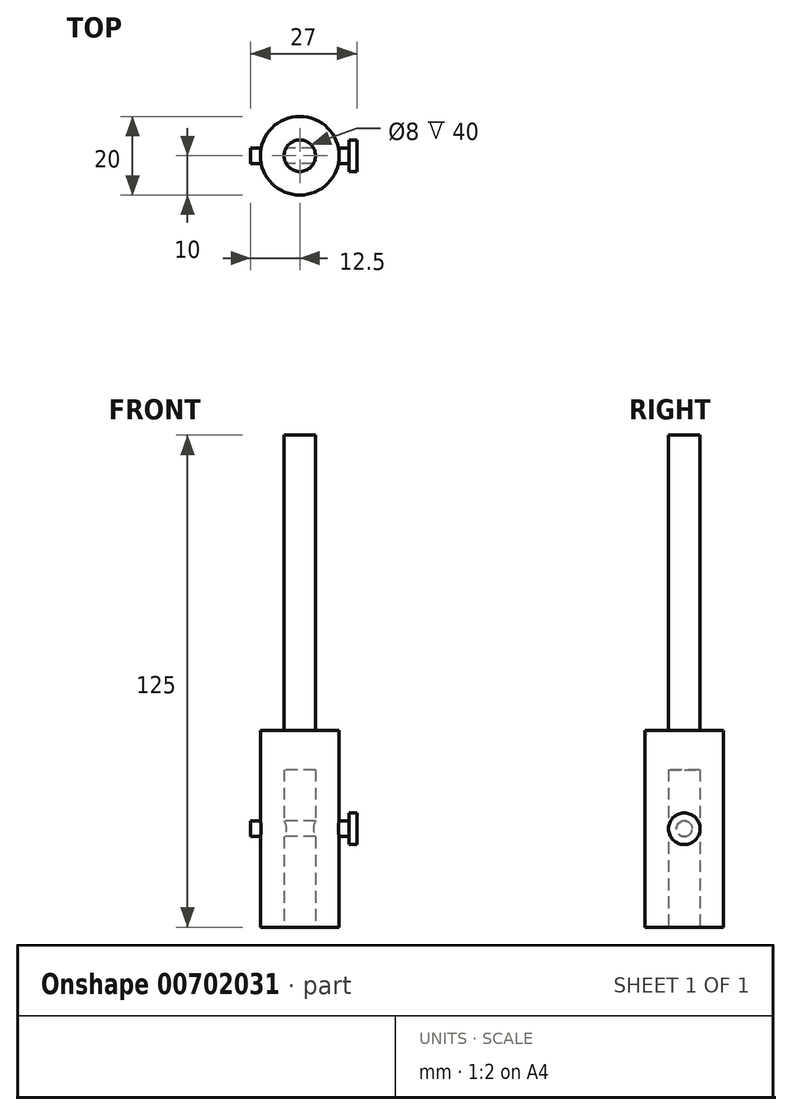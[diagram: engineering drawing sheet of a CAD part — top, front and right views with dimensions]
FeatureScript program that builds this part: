
annotation { "Feature Type Name" : "Feature", "Feature Type Description" : "" }
export const myFeature = defineFeature(function(context is Context, id is Id, definition is map)
    precondition{}
    {
        {
            var Q0;
            Q0=qCreatedBy(makeId("Top.planeOp"),FACE);
            var sketch = newSketch(context, id + "F0", { "sketchPlane" : qUnion([Q0])});
            skCircle(sketch, "E0", {"center": v(0, 0) * mm, "radius": 10 * mm});
            skCircle(sketch, "E1", {"center": v(0, 0) * mm, "radius": 4 * mm});
            skSolve(sketch);
        }
        {
            var Q0;
            Q0 = qSketchRegion(id + "F0", true);
            extrude(context, id + "F1", {"entities" : qUnion([Q0]), "endBound" : BoundingType.SYMMETRIC, "depth" : 50 * mm, "offsetDistance" : 25 * mm});
        }
        {
            var Q0;
            Q0=qCreatedBy(makeId("Right.planeOp"),FACE);
            var sketch = newSketch(context, id + "F2", { "sketchPlane" : qUnion([Q0])});
            skCircle(sketch, "E2", {"center": v(0, 0) * mm, "radius": 2 * mm});
            skSolve(sketch);
        }
        {
            var Q0;
            Q0 = qSketchRegion(id + "F2", true);
            extrude(context, id + "F3", {"entities" : qUnion([Q0]), "operationType" : NewBodyOperationType.ADD, "endBound" : BoundingType.SYMMETRIC, "depth" : 25 * mm, "offsetDistance" : 25 * mm, "hasSecondDirection" : true, "secondDirectionOppositeDirection" : false, "secondDirectionDepth" : 8 * mm});
        }
        {
            var Q0;
            Q0=qCreatedBy(makeId("Right.planeOp"),FACE);
            var sketch = newSketch(context, id + "F4", { "sketchPlane" : qUnion([Q0])});
            skCircle(sketch, "E3", {"center": v(0, 0) * mm, "radius": 4 * mm});
            skSolve(sketch);
        }
        {
            var Q0;
            Q0 = qSketchRegion(id + "F4", true);
            extrude(context, id + "F5", {"entities" : qUnion([Q0]), "operationType" : NewBodyOperationType.ADD, "depth" : 14.5 * mm, "offsetDistance" : 25 * mm, "hasSecondDirection" : true, "secondDirectionOppositeDirection" : false, "secondDirectionDepth" : 12.5 * mm});
        }
        {
            var Q0;
            Q0=qCreatedBy(makeId("Top.planeOp"),FACE);
            var sketch = newSketch(context, id + "F6", { "sketchPlane" : qUnion([Q0])});
            skCircle(sketch, "E4", {"center": v(0, 0) * mm, "radius": 4 * mm});
            skSolve(sketch);
        }
        {
            var Q0;
            Q0 = qSketchRegion(id + "F6", true);
            extrude(context, id + "F7", {"entities" : qUnion([Q0]), "operationType" : NewBodyOperationType.ADD, "depth" : 100 * mm, "offsetDistance" : 25 * mm, "hasSecondDirection" : true, "secondDirectionOppositeDirection" : false, "secondDirectionDepth" : 15 * mm});
        }
    });
